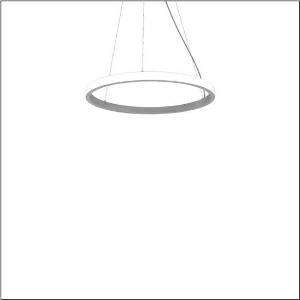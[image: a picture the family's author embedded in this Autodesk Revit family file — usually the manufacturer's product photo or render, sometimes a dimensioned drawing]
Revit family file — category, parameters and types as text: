
# Revit family: silica_r__21_ring-o_5pjbo2d1204a_bf82
name_source: partatom
category: Lighting Fixtures
units: mm (PartAtom-declared; Revit-internal decimal feet)

## family parameters
Cut with Voids When Loaded = No
Host = Face
Light Source = No
Part Type = Normal
Room Calculation Point = No
Round Connector Dimension = Use Diameter
Shared = No

## types (1)
- Silica® 21 Ring-O (1 x LED, 4700 lm, 80 W, 3000K)
    Apparent Load = 80 VA
    CIE Flux Codes = 2 16 49 50 100
    Color Rendering = 80
    Color Temperature = 3000K
    Default Elevation = 1800 mm
    Description = Silica® 21 Ring-O, suspended luminaire, of PMMA, frosted, light emission: outer ring side luminous distribution, primary light characteristic: symmetric, installation type: suspended mounting, LED, rated luminous flux: 4.700lm, luminous efficacy: 59lm/W, light colour: 830, colour temperature: 3000K, control gear: DALI 2, with terminal, 5-pole, mains connection: 230V, AC/DC, 0/50..60Hz, rated input power: 80W, housing, of extruded aluminium section, metallic grey (RAL 9006), diameter: 810mm, ceiling canopy, metallic grey (RAL 9006), protection rating (lamp compartment): IP40, insulation class (complete): insulation class I (protective earthing), certification: CE, impact resistance: IK02, permissible operating ambient temperature: 0..+35°C, packaging unit: 1 piece
    Height = 48 mm  [stored 0.15748 ft]
    Lamp = 1 x LED
    Lamp Light Flux = 4700 lm
    Lamp Power = 80 W
    Lamp count = 1
    Length = 810 mm
    Luminous efficacy = 59 lm/W
    Manufacturer = Siteco
    ModVariant = No
    Model = 5PJBO2D1204A
    Mounting Place = Ceiling
    Mounting Type = Pendant
    Number of Poles = 1
    OnlyDefault = Yes
    Power Factor = 1
    Product Name = Silica® 21 Ring-O
    Product group = suspended luminaire
    ProductGroupID = 905
    Protection Class = Protection class I
    Protection Degree = IP 40
    RLX_Detail_Level = 1
    RLX_Emergency_Light_Flux = 0 lm
    RLX_Emergency_Type = 0
    RLX_Emergency_Type_DB = No
    RlxData = <blob elided: 13081 chars, md5=026ae0aa>
    Socket = socket
    Standby Power = 0 W
    System Light Flux = 4700 lm
    System Power = 80 W
    Type Comments = Product without accessories
    Type Image = l_1251760.jpg
    URL = http://relux.com
    VarID = ---
    Voltage = 0 V
    Weight = 0.00 kg
    Width = 0 mm  [stored 0 ft]

note: [stored X ft] marks values corroborated as IEEE doubles in the binary element streams (Revit-internal decimal feet)

## geometry (parser evidence)
native form markers: Sweep x11
no freeform markers — native parametric forms only
